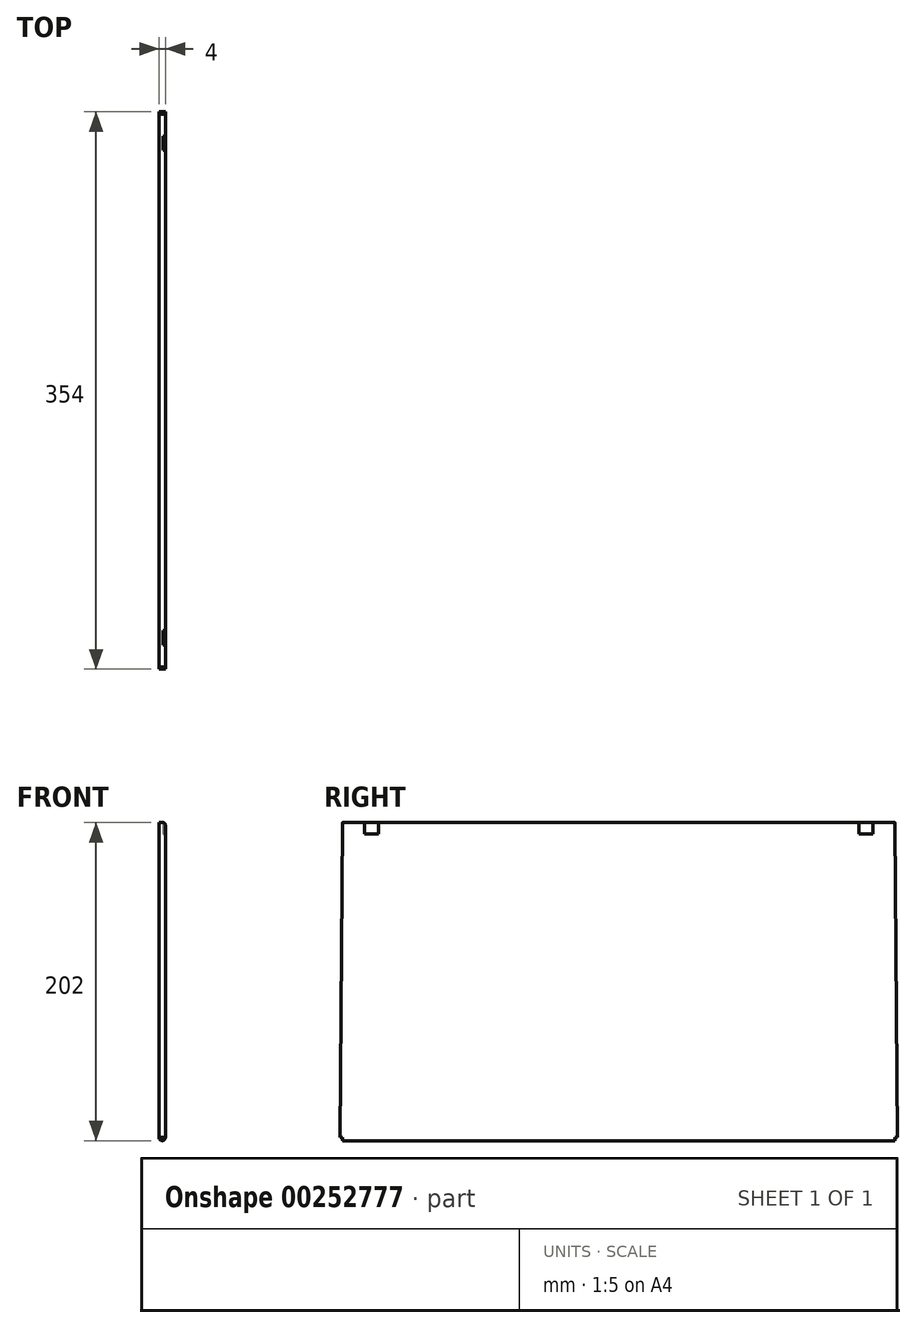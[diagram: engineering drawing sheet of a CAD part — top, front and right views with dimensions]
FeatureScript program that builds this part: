
annotation { "Feature Type Name" : "Feature", "Feature Type Description" : "" }
export const myFeature = defineFeature(function(context is Context, id is Id, definition is map)
    precondition{}
    {
        {
            var Q0;
            Q0=qCreatedBy(makeId("Right.planeOp"),FACE);
            var sketch = newSketch(context, id + "F0", { "sketchPlane" : qUnion([Q0])});
            skLineSegment(sketch, "E0.bottom", {"start": v(-79.1, -89.92) * mm, "end": v(170.84, -89.92) * mm});
            skLineSegment(sketch, "E0.top", {"start": v(-79.1, 0) * mm, "end": v(170.84, 0) * mm});
            skLineSegment(sketch, "E0.left", {"start": v(-79.1, -89.92) * mm, "end": v(-79.1, 0) * mm});
            skLineSegment(sketch, "E0.right", {"start": v(170.84, -89.92) * mm, "end": v(170.84, 0) * mm});
            skSolve(sketch);
        }
        {
            var Q0;
            Q0=makeQuery(id+"F0.imprint","IMPRINT",FACE,{"disambiguationData":[TD([[makeQuery(id+"F0.imprint","IMPRINT",EDGE,{"derivedFrom":sQuery(id+"F0.wireOp",EDGE,"E0.bottom")}),1.0]])]});
            var sketch = newSketch(context, id + "F1", { "sketchPlane" : qUnion([Q0])});
            skLineSegment(sketch, "E1.bottom", {"start": v(171.1, 0) * mm, "end": v(-78.84, 0) * mm});
            skLineSegment(sketch, "E1.top", {"start": v(171.1, 89.92) * mm, "end": v(-78.84, 89.92) * mm});
            skLineSegment(sketch, "E1.left", {"start": v(171.1, 0) * mm, "end": v(171.1, 89.92) * mm});
            skLineSegment(sketch, "E1.right", {"start": v(-78.84, 0) * mm, "end": v(-78.84, 89.92) * mm});
            skSolve(sketch);
        }
        {
            var Q0;
            Q0=makeQuery(id+"F1.imprint","IMPRINT",FACE,{"disambiguationData":[TD([[makeQuery(id+"F1.imprint","IMPRINT",EDGE,{"derivedFrom":sQuery(id+"F1.wireOp",EDGE,"E1.top")}),1.0]])]});
            var Q1;
            Q1=makeQuery(id+"F0.imprint","IMPRINT",FACE,{"disambiguationData":[TD([[makeQuery(id+"F0.imprint","IMPRINT",EDGE,{"derivedFrom":sQuery(id+"F0.wireOp",EDGE,"E0.bottom")}),1.0]])]});
            extrude(context, id + "F2", {"entities" : qUnion([Q0, Q1]), "endBound" : BoundingType.SYMMETRIC, "depth" : 4 * mm});
        }
        {
            var Q0;
            Q0=makeQuery(id+"F2.opExtrude","SWEPT_BODY",BODY,{"disambiguationData":[OSD([sQuery(id+"F1.wireOp",EDGE,"E1.bottom"),sQuery(id+"F1.wireOp",EDGE,"E1.top"),sQuery(id+"F1.wireOp",EDGE,"E1.left"),sQuery(id+"F1.wireOp",EDGE,"E1.right")])]});
            deleteBodies(context, id + "F3", {"entities" : qUnion([Q0])});
        }
        {
            var Q0;
            Q0=makeQuery(id+"F2.opExtrude","SWEPT_BODY",BODY,{"disambiguationData":[OSD([sQuery(id+"F0.wireOp",EDGE,"E0.bottom"),sQuery(id+"F0.wireOp",EDGE,"E0.top"),sQuery(id+"F0.wireOp",EDGE,"E0.left"),sQuery(id+"F0.wireOp",EDGE,"E0.right")])]});
            deleteBodies(context, id + "F4", {"entities" : qUnion([Q0])});
        }
        {
            var Q0;
            Q0=qCreatedBy(makeId("Right.planeOp"),FACE);
            var sketch = newSketch(context, id + "F5", { "sketchPlane" : qUnion([Q0])});
            skLineSegment(sketch, "E2.bottom", {"start": v(-175.5, 100) * mm, "end": v(175.5, 100) * mm});
            skLineSegment(sketch, "E2.top", {"start": v(-175.5, -100) * mm, "end": v(175.5, -100) * mm});
            skLineSegment(sketch, "E2.left", {"start": v(-175.5, 100) * mm, "end": v(-175.5, -100) * mm});
            skLineSegment(sketch, "E2.right", {"start": v(175.5, 100) * mm, "end": v(175.5, -100) * mm});
            skPoint(sketch, "E2.middle", {"position": v(0, 0) * mm});
            skSolve(sketch);
        }
        {
            var Q0;
            Q0=makeQuery(id+"F5.imprint","IMPRINT",FACE,{"disambiguationData":[TD([[makeQuery(id+"F5.imprint","IMPRINT",EDGE,{"derivedFrom":sQuery(id+"F5.wireOp",EDGE,"E2.bottom")}),-1.0]])]});
            extrude(context, id + "F6", {"entities" : qUnion([Q0]), "endBound" : BoundingType.SYMMETRIC, "depth" : 4 * mm});
        }
        {
            var Q0;
            Q0=makeQuery(id+"F6.opExtrude","SWEPT_FACE",FACE,{"disambiguationData":[OSD([sQuery(id+"F5.wireOp",EDGE,"E2.left")])]});
            var sketch = newSketch(context, id + "F7", { "sketchPlane" : qUnion([Q0])});
            skCircle(sketch, "E3", {"center": v(0, -100) * mm, "radius": 2 * mm});
            skSolve(sketch);
        }
        {
            var Q0;
            Q0 = qSketchRegion(id + "F7", true);
            var Q1;
            Q1=makeQuery(id+"F6.opExtrude","SWEPT_FACE",FACE,{"disambiguationData":[OSD([sQuery(id+"F5.wireOp",EDGE,"E2.right")])]});
            extrude(context, id + "F8", {"entities" : qUnion([Q0]), "operationType" : NewBodyOperationType.ADD, "endBound" : BoundingType.UP_TO_SURFACE, "oppositeDirection" : true, "endBoundEntityFace" : qUnion([Q1]), "depth" : 350 * mm});
        }
        {
            var Q0;
            Q0=makeQuery(id+"F6.opExtrude","CAP_FACE",FACE,{"disambiguationData":[OSD([sQuery(id+"F5.wireOp",EDGE,"E2.bottom"),sQuery(id+"F5.wireOp",EDGE,"E2.top"),sQuery(id+"F5.wireOp",EDGE,"E2.left"),sQuery(id+"F5.wireOp",EDGE,"E2.right")])],"isStart":false});
            var sketch = newSketch(context, id + "F9", { "sketchPlane" : qUnion([Q0])});
            skLineSegment(sketch, "E4.bottom", {"start": v(-161.53, 100.74) * mm, "end": v(-152.53, 100.74) * mm});
            skLineSegment(sketch, "E4.top", {"start": v(-161.53, 92.74) * mm, "end": v(-152.53, 92.74) * mm});
            skLineSegment(sketch, "E4.left", {"start": v(-161.53, 100.74) * mm, "end": v(-161.53, 92.74) * mm});
            skLineSegment(sketch, "E4.right", {"start": v(-152.53, 100.74) * mm, "end": v(-152.53, 92.74) * mm});
            skPoint(sketch, "E4.middle", {"position": v(0, 86) * mm});
            skLineSegment(sketch, "E5", {"start": v(-175.5, 86.23) * mm, "end": v(-168.39, 86.23) * mm});
            skLineSegment(sketch, "E6.MirrorCS", {"start": v(161.53, 100.74) * mm, "end": v(161.53, 92.74) * mm});
            skLineSegment(sketch, "E7.MirrorCS", {"start": v(152.53, 100.74) * mm, "end": v(152.53, 92.74) * mm});
            skLineSegment(sketch, "E8.MirrorCS", {"start": v(161.53, 92.74) * mm, "end": v(152.53, 92.74) * mm});
            skLineSegment(sketch, "E9.MirrorCS", {"start": v(161.53, 100.74) * mm, "end": v(152.53, 100.74) * mm});
            skSolve(sketch);
        }
        {
            var Q0;
            {var subQ0=sQuery(id+"F9.wireOp",EDGE,"E4.top");Q0=makeQuery(id+"F9.imprint","IMPRINT",FACE,{"disambiguationData":[TD([[makeQuery(id+"F9.imprint","IMPRINT",EDGE,{"derivedFrom":subQ0}),1.0]])]});}
            var Q1;
            {var subQ0=sQuery(id+"F9.wireOp",EDGE,"E8.MirrorCS");Q1=makeQuery(id+"F9.imprint","IMPRINT",FACE,{"disambiguationData":[TD([[makeQuery(id+"F9.imprint","IMPRINT",EDGE,{"derivedFrom":subQ0}),-1.0]])]});}
            extrude(context, id + "F10", {"entities" : qUnion([Q0, Q1]), "operationType" : NewBodyOperationType.REMOVE, "oppositeDirection" : true, "depth" : 1.5 * mm});
        }
        {
            var Q0;
            {var subQ0=sQuery(id+"F5.wireOp",EDGE,"E2.left");var subQ1=sQuery(id+"F5.wireOp",EDGE,"E2.bottom");Q0=makeQuery(id+"F10.boolean.opBoolean","SPLIT",EDGE,{"disambiguationData":[TD([makeQuery(id+"F6.opExtrude","SWEPT_FACE",FACE,{"disambiguationData":[OSD([subQ0])]})])],"derivedFrom":makeQuery(id+"F6.opExtrude","CAP_EDGE",EDGE,{"disambiguationData":[OSD([subQ1])],"isStart":false})});}
            var Q1;
            {var subQ0=sQuery(id+"F5.wireOp",EDGE,"E2.bottom");Q1=makeQuery(id+"F10.boolean.opBoolean","SPLIT",EDGE,{"disambiguationData":[TD([makeQuery(id+"F10.opExtrude","SWEPT_FACE",FACE,{"disambiguationData":[OSD([sQuery(id+"F9.wireOp",EDGE,"E4.right")])]})])],"derivedFrom":makeQuery(id+"F6.opExtrude","CAP_EDGE",EDGE,{"disambiguationData":[OSD([subQ0])],"isStart":false})});}
            var Q2;
            {var subQ0=sQuery(id+"F5.wireOp",EDGE,"E2.bottom");var subQ1=sQuery(id+"F5.wireOp",EDGE,"E2.right");Q2=makeQuery(id+"F10.boolean.opBoolean","SPLIT",EDGE,{"disambiguationData":[TD([makeQuery(id+"F6.opExtrude","SWEPT_FACE",FACE,{"disambiguationData":[OSD([subQ1])]})])],"derivedFrom":makeQuery(id+"F6.opExtrude","CAP_EDGE",EDGE,{"disambiguationData":[OSD([subQ0])],"isStart":false})});}
            fillet(context, id + "F11", {"entities" : qUnion([Q0, Q1, Q2]), "radius" : 1.5 * mm, "tangentPropagation" : true, "allowEdgeOverflow" : false});
        }
        {
            var Q0;
            Q0=makeQuery(id+"F6.opExtrude","CAP_FACE",FACE,{"disambiguationData":[OSD([sQuery(id+"F5.wireOp",EDGE,"E2.bottom"),sQuery(id+"F5.wireOp",EDGE,"E2.top"),sQuery(id+"F5.wireOp",EDGE,"E2.left"),sQuery(id+"F5.wireOp",EDGE,"E2.right")])],"isStart":false});
            var sketch = newSketch(context, id + "F12", { "sketchPlane" : qUnion([Q0])});
            skLineSegment(sketch, "E10", {"start": v(-175.5, -100) * mm, "end": v(-177, -100) * mm});
            skLineSegment(sketch, "E11", {"start": v(-177, -100) * mm, "end": v(-175.5, 98.5) * mm});
            skLineSegment(sketch, "E12.MirrorCS", {"start": v(175.5, -100) * mm, "end": v(177, -100) * mm});
            skLineSegment(sketch, "E13.MirrorCS", {"start": v(177, -100) * mm, "end": v(175.5, 98.5) * mm});
            skSolve(sketch);
        }
        {
            var Q0;
            Q0=makeQuery(id+"F6.opExtrude","SWEPT_BODY",BODY,{"disambiguationData":[OSD([sQuery(id+"F5.wireOp",EDGE,"E2.bottom"),sQuery(id+"F5.wireOp",EDGE,"E2.top"),sQuery(id+"F5.wireOp",EDGE,"E2.left"),sQuery(id+"F5.wireOp",EDGE,"E2.right")])]});
            transform(context, id + "F13", {"entities" : qUnion([Q0]), "transformType" : TransformType.TRANSLATION_3D, "dx" : 0 * mm, "dy" : 0 * mm, "dz" : 0 * mm, "makeCopy" : true});
        }
        {
            var Q0;
            Q0=makeQuery(id+"F13.opPattern","COPY",BODY,{"derivedFrom":makeQuery(id+"F6.opExtrude","SWEPT_BODY",BODY,{"disambiguationData":[OSD([sQuery(id+"F5.wireOp",EDGE,"E2.bottom"),sQuery(id+"F5.wireOp",EDGE,"E2.top"),sQuery(id+"F5.wireOp",EDGE,"E2.left"),sQuery(id+"F5.wireOp",EDGE,"E2.right")])]}),"instanceName":"1"});
            deleteBodies(context, id + "F14", {"entities" : qUnion([Q0])});
        }
        {
            var Q0;
            Q0=makeQuery(id+"F6.opExtrude","SWEPT_BODY",BODY,{"disambiguationData":[OSD([sQuery(id+"F5.wireOp",EDGE,"E2.bottom"),sQuery(id+"F5.wireOp",EDGE,"E2.top"),sQuery(id+"F5.wireOp",EDGE,"E2.left"),sQuery(id+"F5.wireOp",EDGE,"E2.right")])]});
            transform(context, id + "F15", {"entities" : qUnion([Q0]), "transformType" : TransformType.TRANSLATION_3D, "dx" : 0 * mm, "dy" : 0 * mm, "dz" : 0 * mm, "makeCopy" : true});
        }
        {
            var Q0;
            Q0=makeQuery(id+"F12.imprint","IMPRINT",FACE,{"disambiguationData":[TD([[makeQuery(id+"F12.imprint","IMPRINT",EDGE,{"derivedFrom":sQuery(id+"F12.wireOp",EDGE,"E10")}),-1.0]])]});
            extrude(context, id + "F16", {"entities" : qUnion([Q0]), "operationType" : NewBodyOperationType.ADD, "oppositeDirection" : true, "depth" : 4 * mm});
        }
        {
            var Q0;
            Q0=makeQuery(id+"F12.imprint","IMPRINT",FACE,{"disambiguationData":[TD([[makeQuery(id+"F12.imprint","IMPRINT",EDGE,{"derivedFrom":sQuery(id+"F12.wireOp",EDGE,"E12.MirrorCS")}),1.0]])]});
            extrude(context, id + "F17", {"entities" : qUnion([Q0]), "operationType" : NewBodyOperationType.ADD, "oppositeDirection" : true, "depth" : 4 * mm});
        }
    });
